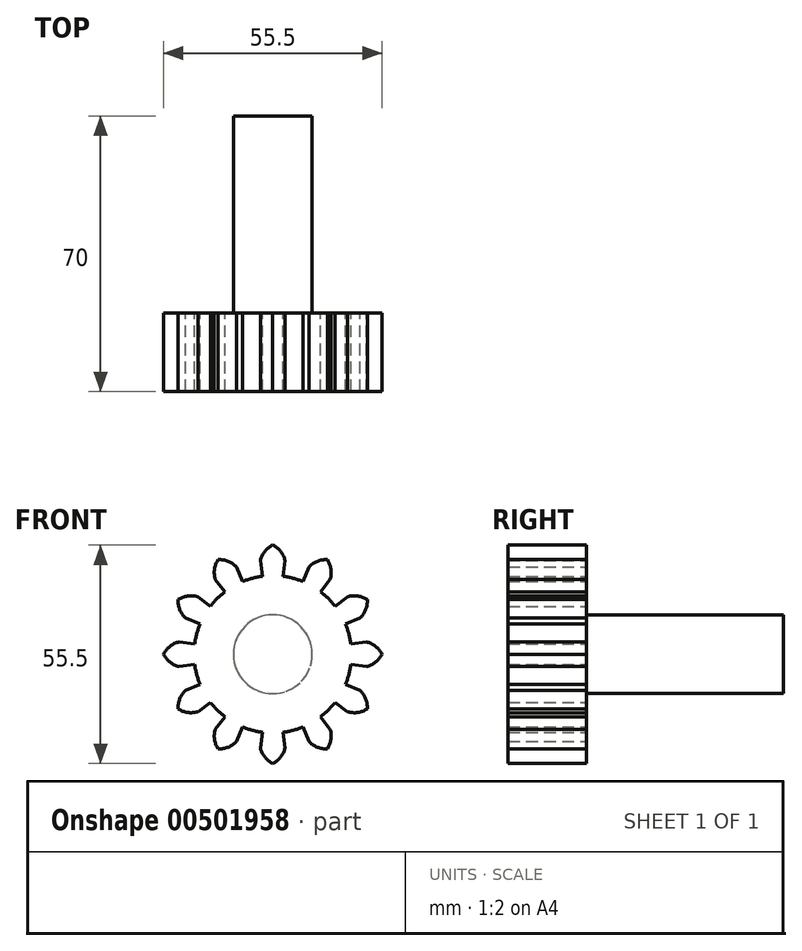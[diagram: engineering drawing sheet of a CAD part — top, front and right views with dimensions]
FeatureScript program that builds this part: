
annotation { "Feature Type Name" : "Feature", "Feature Type Description" : "" }
export const myFeature = defineFeature(function(context is Context, id is Id, definition is map)
    precondition{}
    {
        {
            assignVariable(context, id + "F0", {"name" : "N", "anyValue" : 12});
        }
        {
            var Q0;
            Q0=qCreatedBy(makeId("Front.planeOp"),FACE);
            var sketch = newSketch(context, id + "F1", { "sketchPlane" : qUnion([Q0])});
            skCircle(sketch, "E0", {"center": v(0, 0) * mm, "radius": 20 * mm});
            skCircle(sketch, "E1", {"center": v(0, 0) * mm, "radius": 24 * mm, "construction": true});
            skCircle(sketch, "E2", {"center": v(0, 0) * mm, "radius": 28 * mm, "construction": true});
            skLineSegment(sketch, "E3", {"start": v(3.13, 23.8) * mm, "end": v(-53.59, 31.26) * mm, "construction": true});
            skLineSegment(sketch, "E4", {"start": v(-55.6, 10.77) * mm, "end": v(3.13, 23.8) * mm, "construction": true});
            skCircle(sketch, "E5", {"center": v(0, 0) * mm, "radius": 22.55 * mm, "construction": true});
            skCircle(sketch, "E6", {"center": v(3.13, 23.8) * mm, "radius": 6 * mm, "construction": true});
            skCircle(sketch, "E7", {"center": v(-2.7, 22.4) * mm, "radius": 6 * mm, "construction": true});
            skLineSegment(sketch, "E8", {"start": v(0, 0) * mm, "end": v(-11.02, 83.68) * mm, "construction": true});
            skLineSegment(sketch, "E9", {"start": v(-11.02, 83.68) * mm, "end": v(11.02, 83.68) * mm, "construction": true});
            skLineSegment(sketch, "E10", {"start": v(11.02, 83.68) * mm, "end": v(0, 0) * mm, "construction": true});
            skLineSegment(sketch, "E11", {"start": v(0, 0) * mm, "end": v(0, 83.68) * mm, "construction": true});
            skLineSegment(sketch, "E12", {"start": v(2.61, 19.83) * mm, "end": v(3.13, 23.8) * mm});
            skArc(sketch, "E13", {"start": v(3.13, 23.8) * mm, "mid": v(1.8, 26.35) * mm, "end": v(-0.56, 28) * mm});
            skArc(sketch, "E14", {"start": v(-0.56, 28) * mm, "mid": v(0.28, -28) * mm, "end": v(0, 28) * mm});
            skLineSegment(sketch, "E15.MirrorCS", {"start": v(-2.61, 19.83) * mm, "end": v(-3.13, 23.8) * mm});
            skArc(sketch, "E16.MirrorCS", {"start": v(-3.13, 23.8) * mm, "mid": v(-1.8, 26.35) * mm, "end": v(0.56, 28) * mm});
            skArc(sketch, "E17.MirrorCS", {"start": v(0.56, 28) * mm, "mid": v(-0.28, -28) * mm, "end": v(0, 28) * mm});
            skSolve(sketch);
        }
        {
            var Q0;
            {var subQ0=sQuery(id+"F1.wireOp",EDGE,"E0");var subQ1=makeQuery(id+"F1.imprint","INTERSECT",VERTEX,{"derivedFrom":[subQ0,sQuery(id+"F1.wireOp",EDGE,"E12")]});Q0=makeQuery(id+"F1.imprint","IMPRINT",FACE,{"disambiguationData":[TD([[makeQuery(id+"F1.imprint","IMPRINT",EDGE,{"disambiguationData":[TD([[subQ1,-1.0]])],"derivedFrom":subQ0}),1.0]])]});}
            var Q1;
            {var subQ0=sQuery(id+"F1.wireOp",EDGE,"E12");Q1=makeQuery(id+"F1.imprint","IMPRINT",FACE,{"disambiguationData":[TD([[makeQuery(id+"F1.imprint","IMPRINT",EDGE,{"derivedFrom":subQ0}),1.0]])]});}
            extrude(context, id + "F2", {"entities" : qUnion([Q0, Q1]), "depth" : 20 * mm, "symmetric" : true});
        }
        {
            var Q0;
            Q0=makeQuery(id+"F2.opExtrude","SWEPT_FACE",FACE,{"disambiguationData":[OSD([sQuery(id+"F1.wireOp",EDGE,"E15.MirrorCS")])]});
            var Q1;
            Q1=makeQuery(id+"F2.opExtrude","SWEPT_FACE",FACE,{"disambiguationData":[OSD([sQuery(id+"F1.wireOp",EDGE,"E16.MirrorCS")])]});
            var Q2;
            Q2=makeQuery(id+"F2.opExtrude","SWEPT_FACE",FACE,{"disambiguationData":[OSD([sQuery(id+"F1.wireOp",EDGE,"E14"),sQuery(id+"F1.wireOp",EDGE,"E17.MirrorCS")])]});
            var Q3;
            Q3=makeQuery(id+"F2.opExtrude","SWEPT_FACE",FACE,{"disambiguationData":[OSD([sQuery(id+"F1.wireOp",EDGE,"E13")])]});
            var Q4;
            Q4=makeQuery(id+"F2.opExtrude","SWEPT_FACE",FACE,{"disambiguationData":[OSD([sQuery(id+"F1.wireOp",EDGE,"E12")])]});
            var Q5;
            Q5=makeQuery(id+"F2.opExtrude","SWEPT_FACE",FACE,{"disambiguationData":[OSD([sQuery(id+"F1.wireOp",EDGE,"E0")])]});
            circularPattern(context, id + "F3", {"patternType" : PatternType.FACE, "faces" : qUnion([Q0, Q1, Q2, Q3, Q4]), "axis" : qUnion([Q5]), "angle" : 360 * degree, "instanceCount" : getVariable(context, 'N'), "equalSpace" : true});
        }
        {
            var Q0;
            Q0=makeQuery(id+"F2.opExtrude","CAP_FACE",FACE,{"disambiguationData":[OSD([sQuery(id+"F1.wireOp",EDGE,"E0"),sQuery(id+"F1.wireOp",EDGE,"E12"),sQuery(id+"F1.wireOp",EDGE,"E13"),sQuery(id+"F1.wireOp",EDGE,"E15.MirrorCS"),sQuery(id+"F1.wireOp",EDGE,"E16.MirrorCS")])],"isStart":true});
            var sketch = newSketch(context, id + "F4", { "sketchPlane" : qUnion([Q0])});
            skCircle(sketch, "E18", {"center": v(0, 0) * mm, "radius": 10 * mm});
            skSolve(sketch);
        }
        {
            var Q0;
            Q0=makeQuery(id+"F4.imprint","IMPRINT",FACE,{"disambiguationData":[TD([[makeQuery(id+"F4.imprint","IMPRINT",EDGE,{"derivedFrom":sQuery(id+"F4.wireOp",EDGE,"E18")}),1.0]])]});
            extrude(context, id + "F5", {"entities" : qUnion([Q0]), "operationType" : NewBodyOperationType.ADD, "depth" : 50 * mm});
        }
    });
